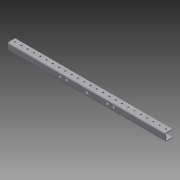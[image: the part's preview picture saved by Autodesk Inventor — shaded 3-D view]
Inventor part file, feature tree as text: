
AUTODESK INVENTOR PART (.ipt)
format: ipt  version: 2011 (Build 150239000, 239)  size: 352,256 bytes
history: native  units: in
note: dims shown in document units (in); Inventor stores cm internally (conversion verified against a paired STEP export)
features: sheet_metal_op x8, sketch x6, other x4, projected_geometry x4, hole x2, pattern_linear x1
ambient origin geometry x8: Origin, YZ Plane, XZ Plane, XY Plane, X Axis, Y Axis, Z Axis, Center Point
feature tree (25):
  sheet_metal_op  "Face2"
  sheet_metal_op  "Flange1"
  sheet_metal_op  "Unfold1"
  hole  "Hole1"  [1 undecoded]
  pattern_linear  "Rectangular Pattern1"  Spacing1=0.125in  [1 undecoded]
  hole  "Hole2"  [1 undecoded]
  sheet_metal_op  "Refold1"
  sheet_metal_op  "Unfold2"
  sheet_metal_op  "Refold2"
  sketch  "Sketch3"  dims[d4=0.75in]
  other  "Plate2"
  sketch  "Sketch4"  dims[d5=0.125in]
  other  "Plate3"
  sheet_metal_op  "Bend1"
  sheet_metal_op  "Corner1"
  sketch  "Sketch6"  dims[d6=0.125in]
  projected_geometry  "Projected Loop1"
  projected_geometry  "Projected Loop2"
  projected_geometry  "Projected Loop3"
  projected_geometry  "Projected Loop4"
  sketch  "Sketch7"  dims[d7=0.0625in]
  sketch  "Sketch8"  dims[d8=0.25in d9=0.125in d10=1.125in d11=90.0deg d12=0.125in d13=0.5in d14=0.125in d15=0.125in d19=0.5in d20=0.5in d21=0.5in d22=0.5in d23=0.257in d24=0.75in d25=0.375in d26=0.25in d27=0.5635in d28=0.125in d29=0.8108in d30=13.7795in d32=1.0in d33=3.25in d34=4.25in d35=13.25in d36=14.25in d37=1.458in d38=1.608in d39=0.38in d40=0.75in d41=0.375in d42=0.25in d43=0.5635in d44=0.125in d45=0.8108in d46=5.0in d47=5.0in d48=0.125in d49=0.0in]
  other  "Cut1"
  other  "Definition1"
  sketch  "Sketch1"  dims[d2=0.125in d3=35.0in]
note: 3 required parameter values undecoded (feature->parameter linkage not recoverable at this tier; creation-order binding heuristic only, values carry confidence <= 0.55)
